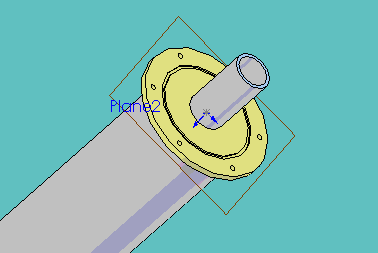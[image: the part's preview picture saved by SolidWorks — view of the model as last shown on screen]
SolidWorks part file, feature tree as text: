
SOLIDWORKS PART (.sldprt)
format: sldprt  version: not decoded by parser v0  size: 181,760 bytes
history: native  units: mm
features: sketch x8, extrude x6, cut_extrude x2, material x1, pattern_circular x1, plane x1 (+11 scaffold rows collapsed)
feature tree (30):
  scaffold x11  (default folders/planes/origin — collapsed)
  material  "Material <not specified>"
  sketch  "Sketch1"  dims[D1=~15.603019mm]
  extrude  "Extrude1"  Depth=73.025mm
  extrude  "Extrude3"  [1 undecoded]
  sketch  "Sketch1<4>"  dims[D1=6.35mm]
  extrude  "Extrude5"  [1 undecoded]
  sketch  "Sketch1<6>"  dims[D1=6.35mm]
  extrude  "Extrude8"  [1 undecoded]
  sketch  "Sketch1<9>"  dims[D1=5.08mm]
  cut_extrude  "Cut-Extrude1"  [1 undecoded]
  sketch  "Sketch1<10>"  dims[D1=1.651mm]
  extrude  "Extrude9"  [1 undecoded]
  sketch  "Sketch1<13>"  dims[D1=6.35mm]
  cut_extrude  "Cut-Extrude5"  [1 undecoded]
  sketch  "Sketch1<14>"  dims[D1=6.35mm]
  pattern_circular  "CirPattern1"  Count=6 Angle=360deg
  plane  "Plane2"  Offset=6.35mm
  sketch  "Sketch5"
  extrude  "Extrude11"  Depth=508mm
decode coverage: 10 of 17 modeling features carry decoded parameters
note: ~ marks probable driven/reference dimensions
note: 6 parameter values undecoded
summary: no parameter record found for 6 features
note: suppression state not decoded; provenance and decode notes live in map.json
